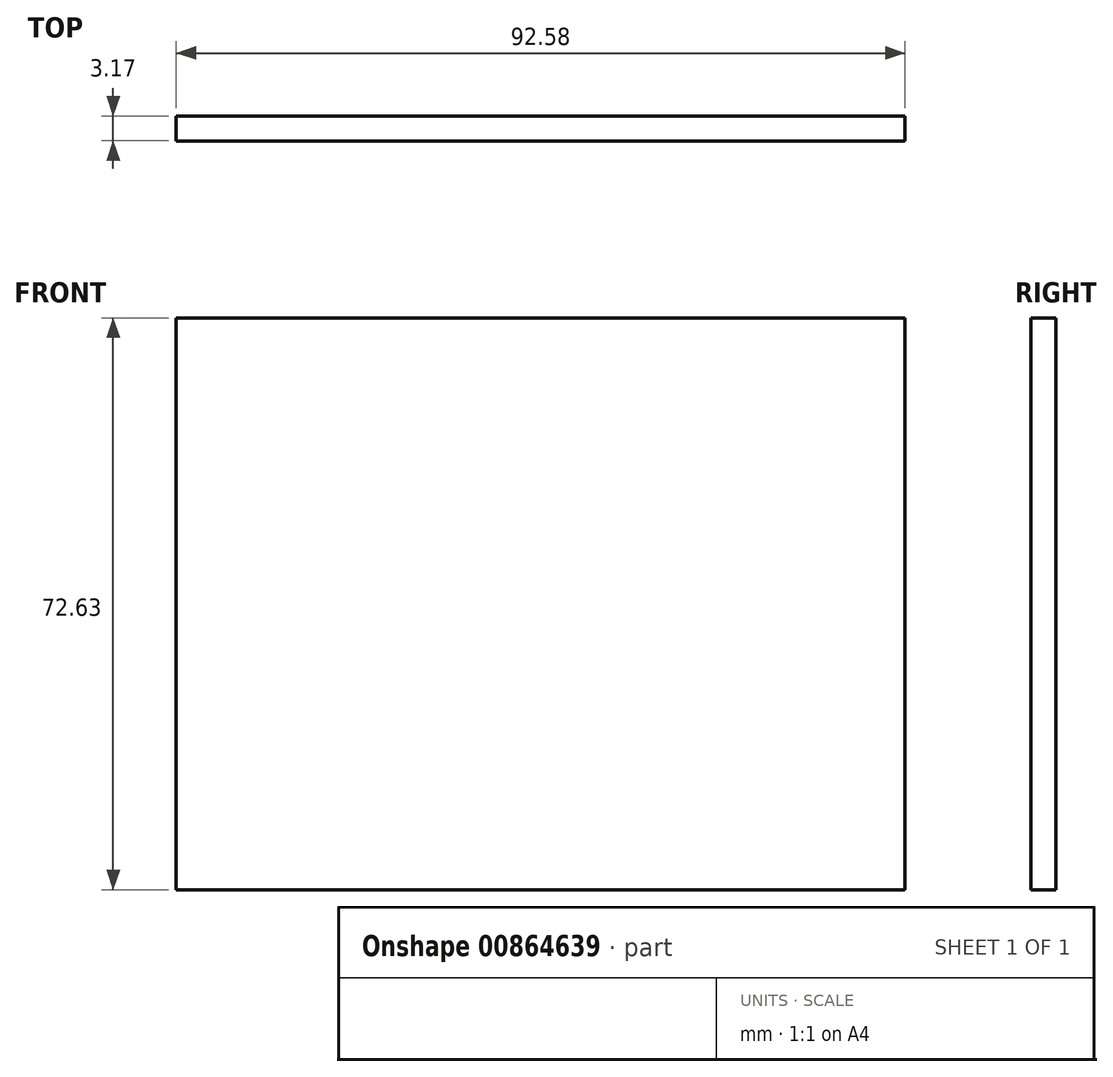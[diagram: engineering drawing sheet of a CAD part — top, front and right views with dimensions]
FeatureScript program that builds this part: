
annotation { "Feature Type Name" : "Feature", "Feature Type Description" : "" }
export const myFeature = defineFeature(function(context is Context, id is Id, definition is map)
    precondition{}
    {
        {
            var Q0;
            Q0=qCreatedBy(makeId("Front.planeOp"),FACE);
            var sketch = newSketch(context, id + "F0", { "sketchPlane" : qUnion([Q0])});
            skLineSegment(sketch, "E0.bottom", {"start": v(-66.33, 50.85) * mm, "end": v(26.25, 50.85) * mm});
            skLineSegment(sketch, "E0.top", {"start": v(-66.33, -21.78) * mm, "end": v(26.25, -21.78) * mm});
            skLineSegment(sketch, "E0.left", {"start": v(-66.33, 50.85) * mm, "end": v(-66.33, -21.78) * mm});
            skLineSegment(sketch, "E0.right", {"start": v(26.25, 50.85) * mm, "end": v(26.25, -21.78) * mm});
            skSolve(sketch);
        }
        {
            var Q0;
            Q0=makeQuery(id+"F0.imprint","IMPRINT",FACE,{"disambiguationData":[TD([[makeQuery(id+"F0.imprint","IMPRINT",EDGE,{"derivedFrom":sQuery(id+"F0.wireOp",EDGE,"E0.bottom")}),-1.0]])]});
            extrude(context, id + "F1", {"entities" : qUnion([Q0]), "depth" : 3.17 * mm, "offsetDistance" : 25.4 * mm});
        }
    });
